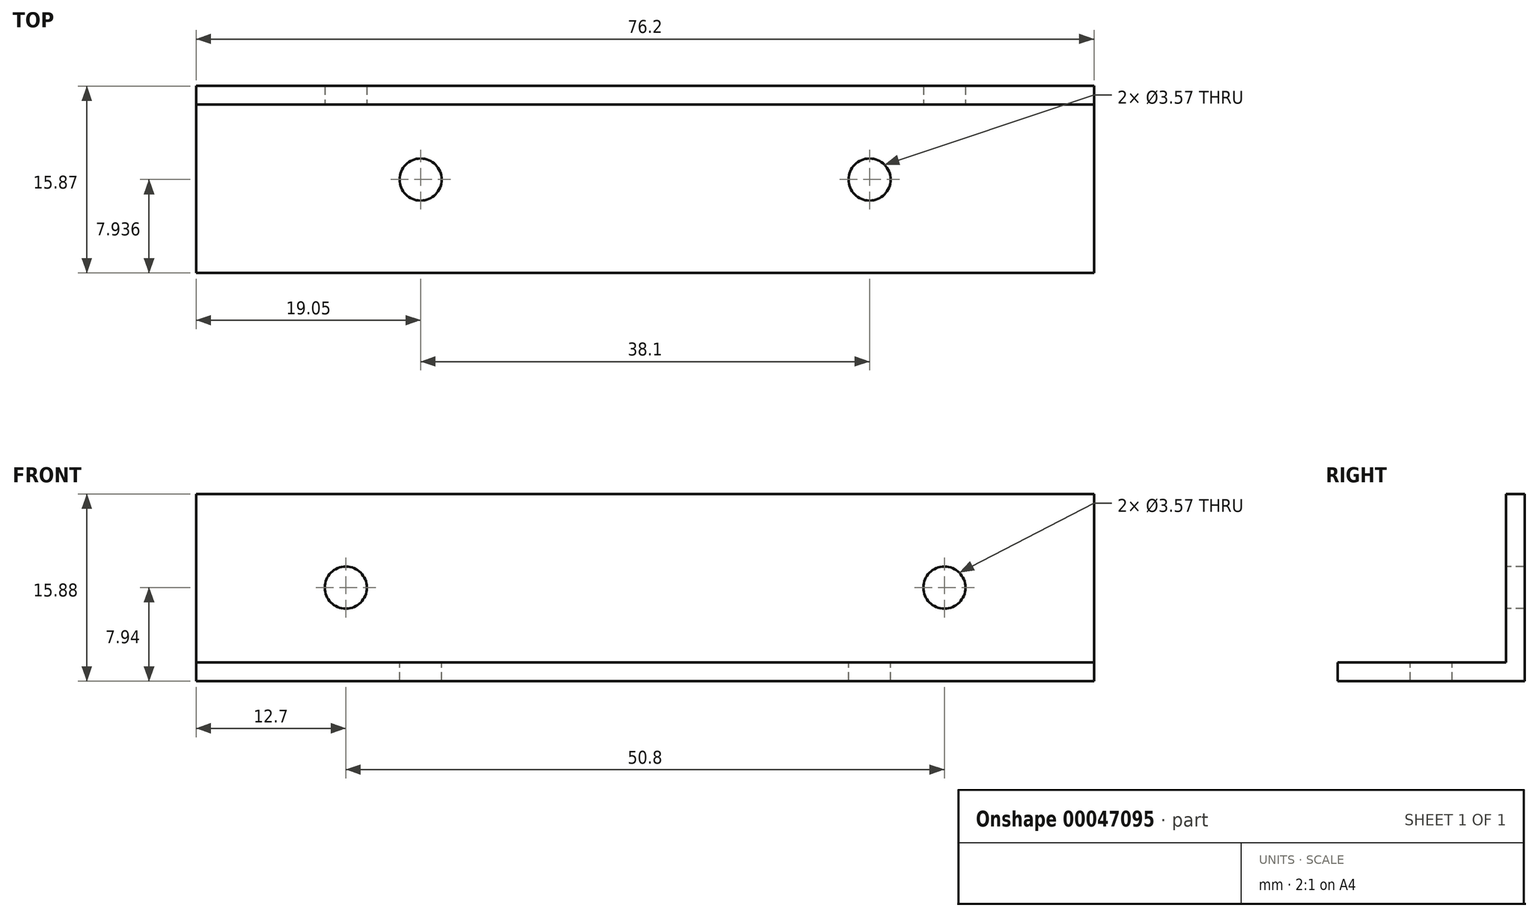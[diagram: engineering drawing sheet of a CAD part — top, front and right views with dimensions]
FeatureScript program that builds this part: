
annotation { "Feature Type Name" : "Feature", "Feature Type Description" : "" }
export const myFeature = defineFeature(function(context is Context, id is Id, definition is map)
    precondition{}
    {
        {
            var Q0;
            Q0=qCreatedBy(makeId("Front.planeOp"),FACE);
            var sketch = newSketch(context, id + "F0", { "sketchPlane" : qUnion([Q0])});
            skLineSegment(sketch, "E0.rect.bottom", {"start": v(38.1, 7.94) * mm, "end": v(-38.1, 7.94) * mm});
            skLineSegment(sketch, "E0.rect.top", {"start": v(38.1, -7.94) * mm, "end": v(-38.1, -7.94) * mm});
            skLineSegment(sketch, "E0.rect.left", {"start": v(38.1, 7.94) * mm, "end": v(38.1, -7.94) * mm});
            skLineSegment(sketch, "E0.rect.right", {"start": v(-38.1, 7.94) * mm, "end": v(-38.1, -7.94) * mm});
            skPoint(sketch, "E0.rect.middle", {"position": v(0, 0) * mm});
            skSolve(sketch);
        }
        {
            var Q0;
            Q0=makeQuery(id+"F0.imprint","IMPRINT",FACE,{"disambiguationData":[TD([[makeQuery(id+"F0.imprint","IMPRINT",EDGE,{"derivedFrom":sQuery(id+"F0.wireOp",EDGE,"E0.rect.bottom")}),1.0]])]});
            extrude(context, id + "F1", {"entities" : qUnion([Q0]), "endBound" : BoundingType.SYMMETRIC, "depth" : 1.59 * mm});
        }
        {
            var Q0;
            Q0=qCreatedBy(makeId("Front.planeOp"),FACE);
            var sketch = newSketch(context, id + "F2", { "sketchPlane" : qUnion([Q0])});
            skCircle(sketch, "E1", {"center": v(-25.4, 0) * mm, "radius": 1.79 * mm});
            skCircle(sketch, "E2", {"center": v(25.4, 0) * mm, "radius": 1.79 * mm});
            skSolve(sketch);
        }
        {
            var Q0;
            Q0 = qSketchRegion(id + "F2", true);
            extrude(context, id + "F3", {"entities" : qUnion([Q0]), "operationType" : NewBodyOperationType.REMOVE, "endBound" : BoundingType.SYMMETRIC, "oppositeDirection" : true, "depth" : 1.59 * mm});
        }
        {
            var Q0;
            Q0=makeQuery(id+"F1.opExtrude","CAP_FACE",FACE,{"disambiguationData":[OSD([sQuery(id+"F0.wireOp",EDGE,"E0.rect.bottom"),sQuery(id+"F0.wireOp",EDGE,"E0.rect.top"),sQuery(id+"F0.wireOp",EDGE,"E0.rect.left"),sQuery(id+"F0.wireOp",EDGE,"E0.rect.right")])],"isStart":false});
            var sketch = newSketch(context, id + "F4", { "sketchPlane" : qUnion([Q0])});
            skLineSegment(sketch, "E3.bottom", {"start": v(-38.1, -7.94) * mm, "end": v(38.1, -7.94) * mm});
            skLineSegment(sketch, "E3.top", {"start": v(-38.1, -6.35) * mm, "end": v(38.1, -6.35) * mm});
            skLineSegment(sketch, "E3.left", {"start": v(-38.1, -7.94) * mm, "end": v(-38.1, -6.35) * mm});
            skLineSegment(sketch, "E3.right", {"start": v(38.1, -7.94) * mm, "end": v(38.1, -6.35) * mm});
            skSolve(sketch);
        }
        {
            var Q0;
            Q0=makeQuery(id+"F4.imprint","IMPRINT",FACE,{"disambiguationData":[TD([[makeQuery(id+"F4.imprint","IMPRINT",EDGE,{"derivedFrom":sQuery(id+"F4.wireOp",EDGE,"E3.bottom")}),-1.0]])]});
            extrude(context, id + "F5", {"entities" : qUnion([Q0]), "operationType" : NewBodyOperationType.ADD, "depth" : 14.29 * mm});
        }
        {
            var Q0;
            Q0=makeQuery(id+"F5.opExtrude","SWEPT_FACE",FACE,{"disambiguationData":[OSD([sQuery(id+"F4.wireOp",EDGE,"E3.top")])]});
            var sketch = newSketch(context, id + "F6", { "sketchPlane" : qUnion([Q0])});
            skCircle(sketch, "E4", {"center": v(-19.05, -7.14) * mm, "radius": 1.79 * mm});
            skCircle(sketch, "E5", {"center": v(19.05, -7.14) * mm, "radius": 1.79 * mm});
            skSolve(sketch);
        }
        {
            var Q0;
            Q0 = qSketchRegion(id + "F6", true);
            extrude(context, id + "F7", {"entities" : qUnion([Q0]), "operationType" : NewBodyOperationType.REMOVE, "endBound" : BoundingType.THROUGH_ALL, "oppositeDirection" : true, "depth" : 25.4 * mm});
        }
    });
